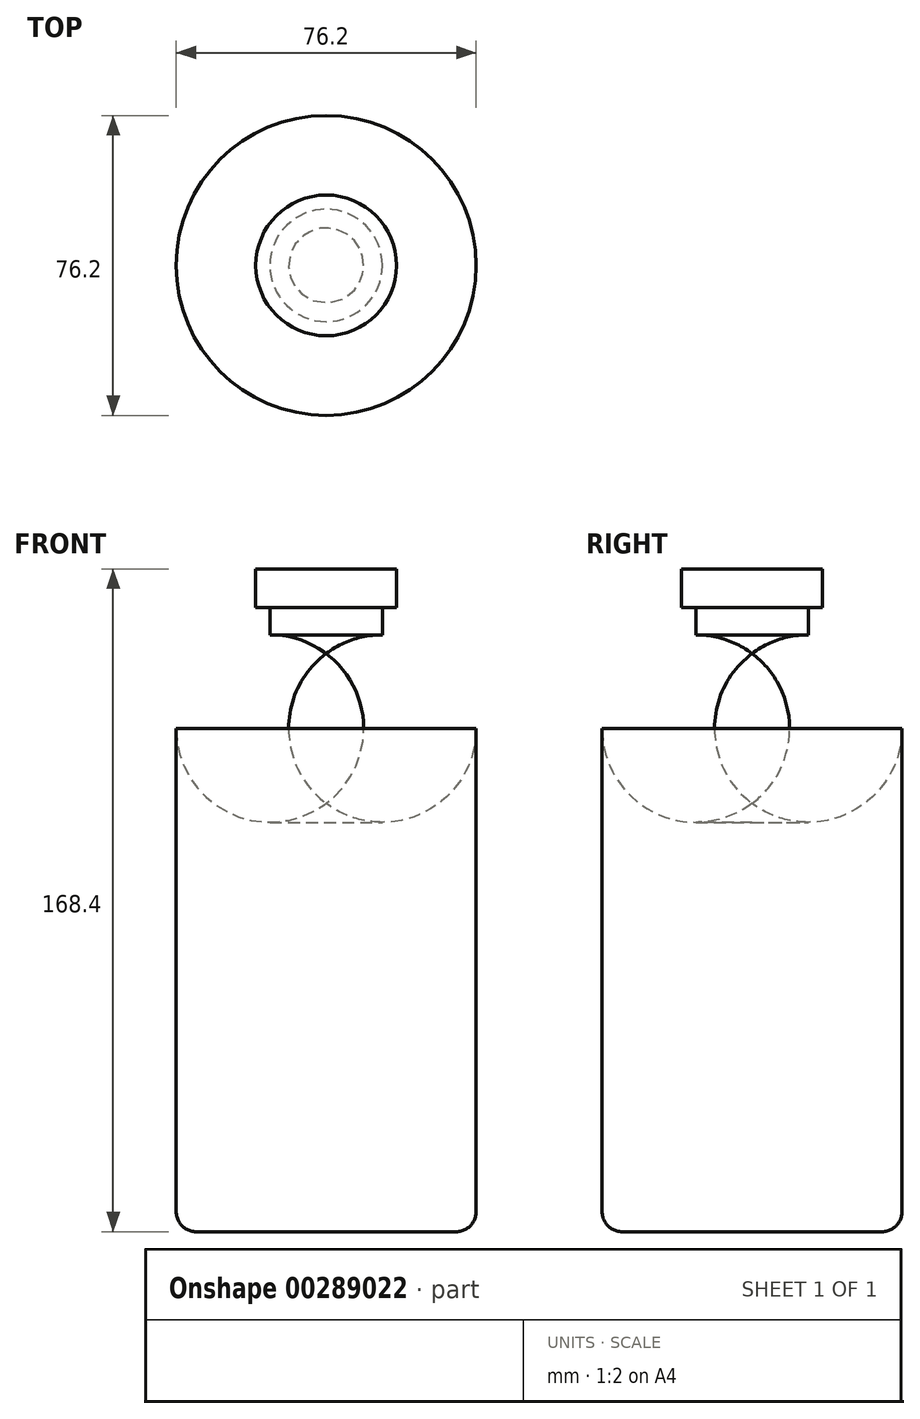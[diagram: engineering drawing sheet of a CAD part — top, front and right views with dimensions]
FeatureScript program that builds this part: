
annotation { "Feature Type Name" : "Feature", "Feature Type Description" : "" }
export const myFeature = defineFeature(function(context is Context, id is Id, definition is map)
    precondition{}
    {
        {
            var Q0;
            Q0=qCreatedBy(makeId("Front.planeOp"),FACE);
            var sketch = newSketch(context, id + "F0", { "sketchPlane" : qUnion([Q0])});
            skLineSegment(sketch, "E0", {"start": v(0, 0) * mm, "end": v(0, 168.4) * mm});
            skLineSegment(sketch, "E1", {"start": v(0, 0) * mm, "end": v(-38.1, 0) * mm});
            skLineSegment(sketch, "E2", {"start": v(-38.1, 0) * mm, "end": v(-38.1, 127.84) * mm});
            skLineSegment(sketch, "E3", {"start": v(0, 168.4) * mm, "end": v(-17.88, 168.4) * mm});
            skLineSegment(sketch, "E4", {"start": v(-17.88, 168.4) * mm, "end": v(-17.88, 158.57) * mm});
            skLineSegment(sketch, "E5", {"start": v(-17.88, 158.57) * mm, "end": v(-14.29, 158.57) * mm});
            skLineSegment(sketch, "E6", {"start": v(-14.29, 158.57) * mm, "end": v(-14.29, 151.65) * mm});
            skArc(sketch, "E7", {"start": v(-14.29, 151.65) * mm, "mid": v(-31.13, 144.68) * mm, "end": v(-38.1, 127.84) * mm});
            skLineSegment(sketch, "E8", {"start": v(-14.29, 151.65) * mm, "end": v(0, 151.65) * mm, "construction": true});
            skSolve(sketch);
        }
        {
            var Q0;
            Q0=makeQuery(id+"F0.imprint","IMPRINT",FACE,{"disambiguationData":[TD([[makeQuery(id+"F0.imprint","IMPRINT",EDGE,{"derivedFrom":sQuery(id+"F0.wireOp",EDGE,"E0")}),1.0]])]});
            var Q1;
            Q1=sQuery(id+"F0.wireOp",EDGE,"E0");
            revolve(context, id + "F1", {"entities" : qUnion([Q0]), "axis" : qUnion([Q1]), "revolveType" : RevolveType.FULL});
        }
        {
            var Q0;
            Q0=makeQuery(id+"F1.opRevolve","SWEPT_EDGE",EDGE,{"disambiguationData":[OSD([sQuery(id+"F0.wireOp",EDGE,"E1"),sQuery(id+"F0.wireOp",EDGE,"E2")])]});
            fillet(context, id + "F2", {"entities" : qUnion([Q0]), "radius" : 5.08 * mm, "tangentPropagation" : true, "allowEdgeOverflow" : false});
        }
    });
